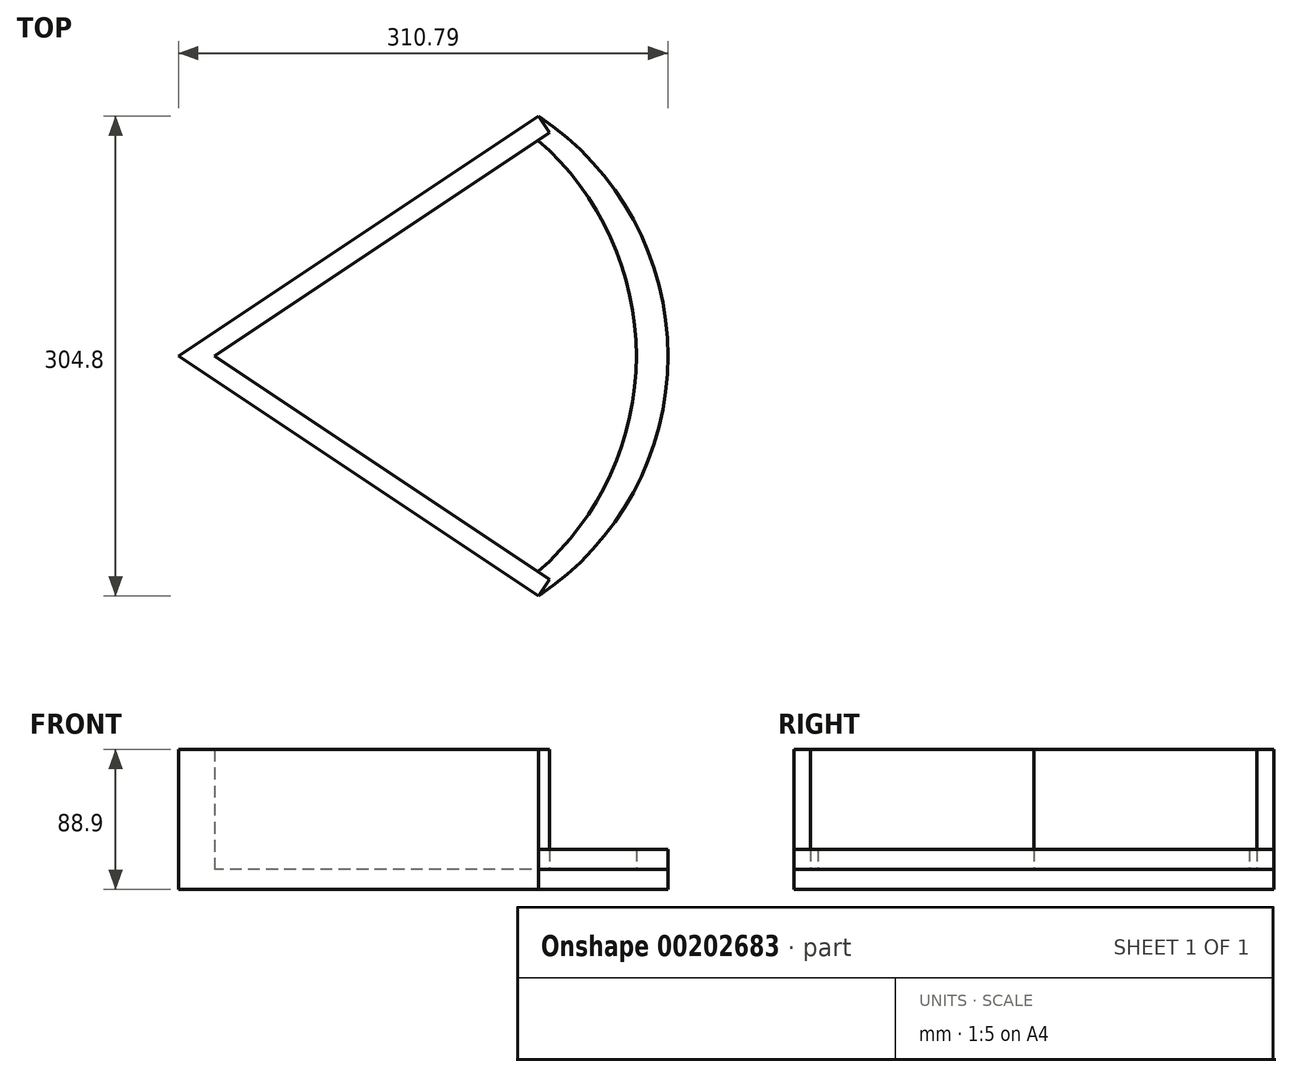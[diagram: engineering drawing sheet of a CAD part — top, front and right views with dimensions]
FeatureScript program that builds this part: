
annotation { "Feature Type Name" : "Feature", "Feature Type Description" : "" }
export const myFeature = defineFeature(function(context is Context, id is Id, definition is map)
    precondition{}
    {
        {
            var Q0;
            Q0=qCreatedBy(makeId("Top.planeOp"),FACE);
            var sketch = newSketch(context, id + "F0", { "sketchPlane" : qUnion([Q0])});
            skLineSegment(sketch, "E0", {"start": v(0, 0) * mm, "end": v(228.6, 0) * mm});
            skLineSegment(sketch, "E1", {"start": v(228.6, 0) * mm, "end": v(228.6, 152.4) * mm});
            skLineSegment(sketch, "E2", {"start": v(228.6, 0) * mm, "end": v(228.6, -152.4) * mm});
            skArc(sketch, "E3", {"start": v(228.6, -152.4) * mm, "mid": v(310.8, 0) * mm, "end": v(228.6, 152.4) * mm});
            skLineSegment(sketch, "E4", {"start": v(0, 0) * mm, "end": v(228.6, -152.4) * mm});
            skLineSegment(sketch, "E5", {"start": v(0, 0) * mm, "end": v(228.6, 152.4) * mm});
            skSolve(sketch);
        }
        {
            var Q0;
            Q0=makeQuery(id+"F0.imprint","IMPRINT",FACE,{"disambiguationData":[TD([[makeQuery(id+"F0.imprint","IMPRINT",EDGE,{"derivedFrom":sQuery(id+"F0.wireOp",EDGE,"E0")}),1.0]])]});
            var Q1;
            Q1=makeQuery(id+"F0.imprint","IMPRINT",FACE,{"disambiguationData":[TD([[makeQuery(id+"F0.imprint","IMPRINT",EDGE,{"derivedFrom":sQuery(id+"F0.wireOp",EDGE,"E0")}),-1.0]])]});
            var Q2;
            Q2=makeQuery(id+"F0.imprint","IMPRINT",FACE,{"disambiguationData":[TD([[makeQuery(id+"F0.imprint","IMPRINT",EDGE,{"derivedFrom":sQuery(id+"F0.wireOp",EDGE,"E1")}),-1.0]])]});
            extrude(context, id + "F1", {"entities" : qUnion([Q0, Q1, Q2]), "depth" : 12.7 * mm});
        }
        {
            var Q0;
            Q0=makeQuery(id+"F1.opExtrude","CAP_FACE",FACE,{"disambiguationData":[OSD([sQuery(id+"F0.wireOp",EDGE,"E3"),sQuery(id+"F0.wireOp",EDGE,"E4"),sQuery(id+"F0.wireOp",EDGE,"E5")])],"isStart":false});
            var sketch = newSketch(context, id + "F2", { "sketchPlane" : qUnion([Q0])});
            skLineSegment(sketch, "E6", {"start": v(228.6, -152.4) * mm, "end": v(235.64, -141.83) * mm});
            skLineSegment(sketch, "E7", {"start": v(235.64, -141.83) * mm, "end": v(11.45, 7.63) * mm});
            skLineSegment(sketch, "E8", {"start": v(228.6, 152.4) * mm, "end": v(235.64, 141.83) * mm});
            skLineSegment(sketch, "E9", {"start": v(235.64, 141.83) * mm, "end": v(22.9, 0) * mm});
            skSolve(sketch);
        }
        {
            var Q0;
            {var subQ4=sQuery(id+"F2.wireOp",EDGE,"E8");Q0=makeQuery(id+"F2.imprint","IMPRINT",FACE,{"disambiguationData":[TD([[makeQuery(id+"F2.imprint","IMPRINT",EDGE,{"derivedFrom":subQ4}),-1.0]])]});}
            var Q1;
            {var subQ5=sQuery(id+"F2.wireOp",EDGE,"E6");Q1=makeQuery(id+"F2.imprint","IMPRINT",FACE,{"disambiguationData":[TD([[makeQuery(id+"F2.imprint","IMPRINT",EDGE,{"derivedFrom":subQ5}),1.0]])]});}
            extrude(context, id + "F3", {"entities" : qUnion([Q0, Q1]), "operationType" : NewBodyOperationType.ADD, "depth" : 76.2 * mm});
        }
        {
            var Q0;
            Q0=makeQuery(id+"F1.opExtrude","CAP_FACE",FACE,{"disambiguationData":[OSD([sQuery(id+"F0.wireOp",EDGE,"E3"),sQuery(id+"F0.wireOp",EDGE,"E4"),sQuery(id+"F0.wireOp",EDGE,"E5")])],"isStart":false});
            var sketch = newSketch(context, id + "F4", { "sketchPlane" : qUnion([Q0])});
            skArc(sketch, "E10", {"start": v(228.6, -152.4) * mm, "mid": v(311.27, 0) * mm, "end": v(228.6, 152.4) * mm});
            skLineSegment(sketch, "E11", {"start": v(228.6, -152.4) * mm, "end": v(218.03, -145.36) * mm});
            skLineSegment(sketch, "E12", {"start": v(228.6, 152.4) * mm, "end": v(218.03, 145.36) * mm});
            skArc(sketch, "E13", {"start": v(218.03, -145.36) * mm, "mid": v(290.77, 0) * mm, "end": v(218.03, 145.36) * mm});
            skSolve(sketch);
        }
        {
            var Q0;
            Q0=makeQuery(id+"F4.imprint","IMPRINT",FACE,{"disambiguationData":[TD([[makeQuery(id+"F4.imprint","IMPRINT",EDGE,{"derivedFrom":makeQuery(id+"F1.opExtrude","CAP_EDGE",EDGE,{"disambiguationData":[OSD([sQuery(id+"F0.wireOp",EDGE,"E3")])],"isStart":false})}),1.0]])]});
            extrude(context, id + "F5", {"entities" : qUnion([Q0]), "depth" : 12.7 * mm});
        }
    });
